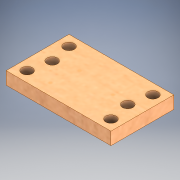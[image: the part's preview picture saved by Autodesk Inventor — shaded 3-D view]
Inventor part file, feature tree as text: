
AUTODESK INVENTOR PART (.ipt)
format: ipt  version: 2020 (Build 240168000, 168)  size: 137,216 bytes
history: native  units: mm
features: extrude x1, sketch x1
ambient origin geometry x8: Origin, YZ Plane, XZ Plane, XY Plane, X Axis, Y Axis, Z Axis, Center Point
bodies: Solide1 (feature_tree)
feature tree (2):
  extrude  "Extrusion1"  Depth=50.0mm
  sketch  "Esquisse1"
